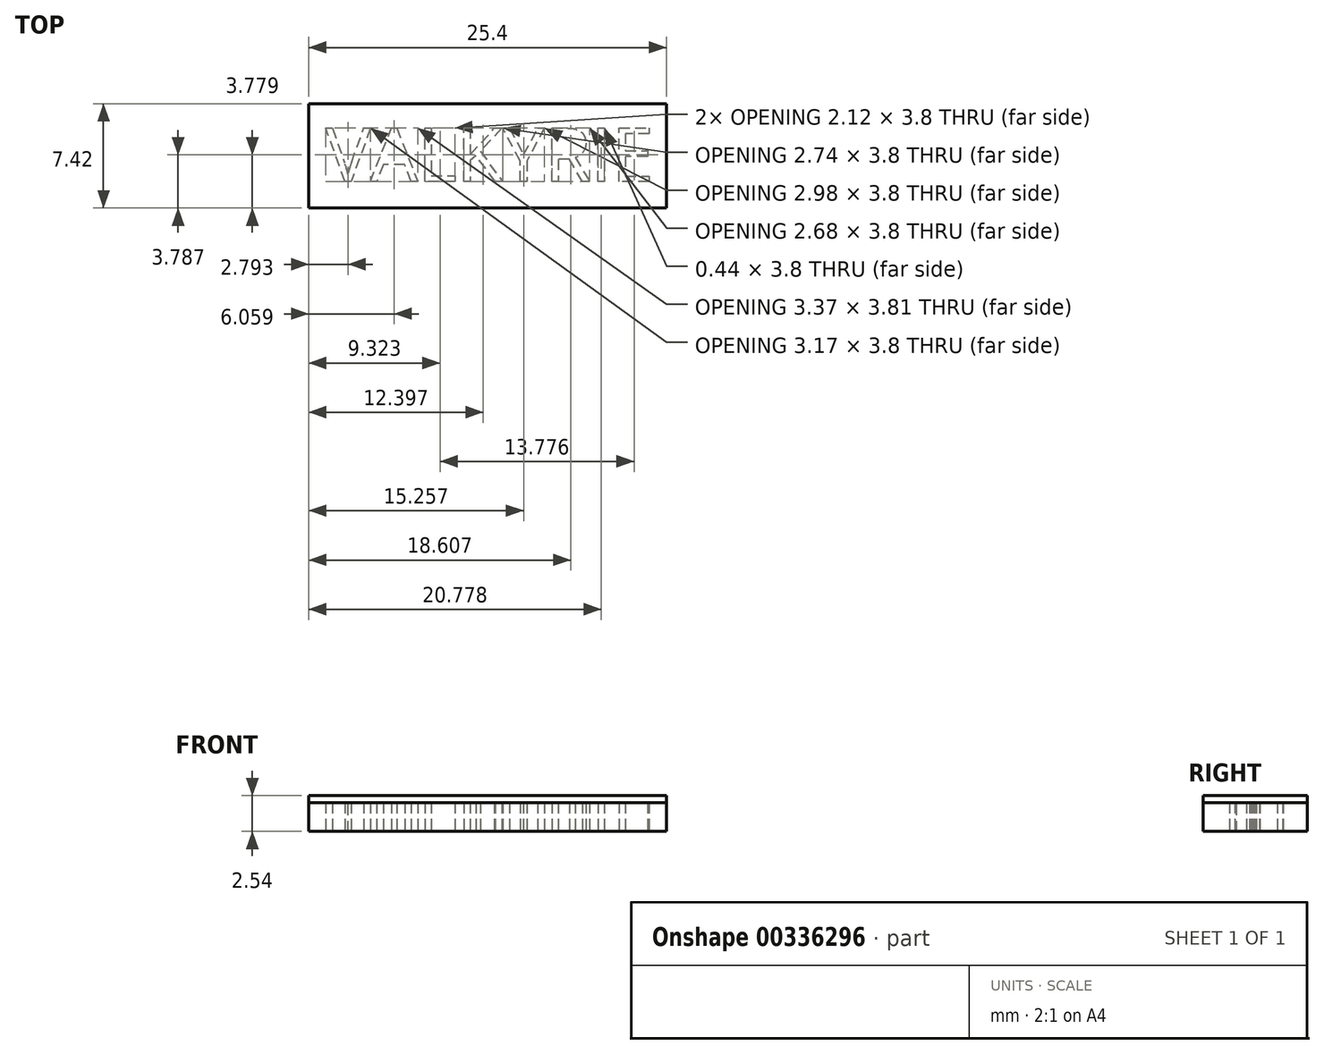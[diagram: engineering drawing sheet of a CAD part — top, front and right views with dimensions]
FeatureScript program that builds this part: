
annotation { "Feature Type Name" : "Feature", "Feature Type Description" : "" }
export const myFeature = defineFeature(function(context is Context, id is Id, definition is map)
    precondition{}
    {
        {
            var Q0;
            Q0=qCreatedBy(makeId("Top.planeOp"),FACE);
            var sketch = newSketch(context, id + "F0", { "sketchPlane" : qUnion([Q0])});
            skText(sketch, "E0", { "text": "VALKYRIE", "fontName": "OpenSans-Regular.ttf"});
            skLineSegment(sketch, "E1.bottom", {"start": v(-24.48, 5.54) * mm, "end": v(0.92, 5.54) * mm});
            skLineSegment(sketch, "E1.top", {"start": v(-24.48, -1.88) * mm, "end": v(0.92, -1.88) * mm});
            skLineSegment(sketch, "E1.left", {"start": v(-24.48, 5.54) * mm, "end": v(-24.48, -1.88) * mm});
            skLineSegment(sketch, "E1.right", {"start": v(0.92, 5.54) * mm, "end": v(0.92, -1.88) * mm});
            const initialGuessF0  = {"E0": [-0.02327, 0, 1, 0, 0.00383]};
            skSetInitialGuess(sketch, initialGuessF0);
            skSolve(sketch);
        }
        {
            var Q0;
            Q0=makeQuery(id+"F0.imprint","IMPRINT",FACE,{"disambiguationData":[TD([[makeQuery(id+"F0.imprint","IMPRINT",EDGE,{"derivedFrom":sQuery(id+"F0.wireOp",EDGE,"E0.sketch_text.stroke-0")}),1.0]])]});
            var Q1;
            Q1 = qSketchRegion(id + "F0", true);
            extrude(context, id + "F1", {"entities" : qUnion([Q0, Q1]), "depth" : 2.03 * mm});
        }
        {
            var Q0;
            Q0=makeQuery(id+"F0.imprint","IMPRINT",FACE,{"disambiguationData":[TD([[makeQuery(id+"F0.imprint","IMPRINT",EDGE,{"derivedFrom":sQuery(id+"F0.wireOp",EDGE,"E0.sketch_text.stroke-0")}),1.0]])]});
            var Q1;
            Q1 = qSketchRegion(id + "F0", true);
            var Q2;
            Q2=makeQuery(id+"F0.imprint","IMPRINT",FACE,{"disambiguationData":[TD([[makeQuery(id+"F0.imprint","IMPRINT",EDGE,{"derivedFrom":sQuery(id+"F0.wireOp",EDGE,"E0.sketch_text.stroke-0")}),-1.0]])]});
            var Q3;
            Q3=makeQuery(id+"F0.imprint","IMPRINT",FACE,{"disambiguationData":[TD([[makeQuery(id+"F0.imprint","IMPRINT",EDGE,{"derivedFrom":sQuery(id+"F0.wireOp",EDGE,"E0.sketch_text.stroke-17")}),1.0]])]});
            var Q4;
            Q4=makeQuery(id+"F0.imprint","IMPRINT",FACE,{"disambiguationData":[TD([[makeQuery(id+"F0.imprint","IMPRINT",EDGE,{"derivedFrom":sQuery(id+"F0.wireOp",EDGE,"E0.sketch_text.stroke-28")}),-1.0]])]});
            var Q5;
            Q5=makeQuery(id+"F0.imprint","IMPRINT",FACE,{"disambiguationData":[TD([[makeQuery(id+"F0.imprint","IMPRINT",EDGE,{"derivedFrom":sQuery(id+"F0.wireOp",EDGE,"E0.sketch_text.stroke-40")}),-1.0]])]});
            var Q6;
            Q6=makeQuery(id+"F0.imprint","IMPRINT",FACE,{"disambiguationData":[TD([[makeQuery(id+"F0.imprint","IMPRINT",EDGE,{"derivedFrom":sQuery(id+"F0.wireOp",EDGE,"E0.sketch_text.stroke-60")}),1.0]])]});
            var Q7;
            Q7=makeQuery(id+"F0.imprint","IMPRINT",FACE,{"disambiguationData":[TD([[makeQuery(id+"F0.imprint","IMPRINT",EDGE,{"derivedFrom":sQuery(id+"F0.wireOp",EDGE,"E0.sketch_text.stroke-67")}),-1.0]])]});
            var Q8;
            Q8=makeQuery(id+"F0.imprint","IMPRINT",FACE,{"disambiguationData":[TD([[makeQuery(id+"F0.imprint","IMPRINT",EDGE,{"derivedFrom":sQuery(id+"F0.wireOp",EDGE,"E0.sketch_text.stroke-71")}),-1.0]])]});
            var Q9;
            Q9=makeQuery(id+"F0.imprint","IMPRINT",FACE,{"disambiguationData":[TD([[makeQuery(id+"F0.imprint","IMPRINT",EDGE,{"derivedFrom":sQuery(id+"F0.wireOp",EDGE,"E0.sketch_text.stroke-49")}),-1.0]])]});
            var Q10;
            Q10=makeQuery(id+"F0.imprint","IMPRINT",FACE,{"disambiguationData":[TD([[makeQuery(id+"F0.imprint","IMPRINT",EDGE,{"derivedFrom":sQuery(id+"F0.wireOp",EDGE,"E0.sketch_text.stroke-9")}),-1.0]])]});
            var Q11;
            Q11=makeQuery(id+"F0.imprint","IMPRINT",FACE,{"disambiguationData":[TD([[makeQuery(id+"F0.imprint","IMPRINT",EDGE,{"derivedFrom":sQuery(id+"F0.wireOp",EDGE,"E0.sketch_text.stroke-22")}),-1.0]])]});
            extrude(context, id + "F2", {"entities" : qUnion([Q0, Q1, Q2, Q3, Q4, Q5, Q6, Q7, Q8, Q9, Q10, Q11]), "depth" : 2.54 * mm});
        }
    });
